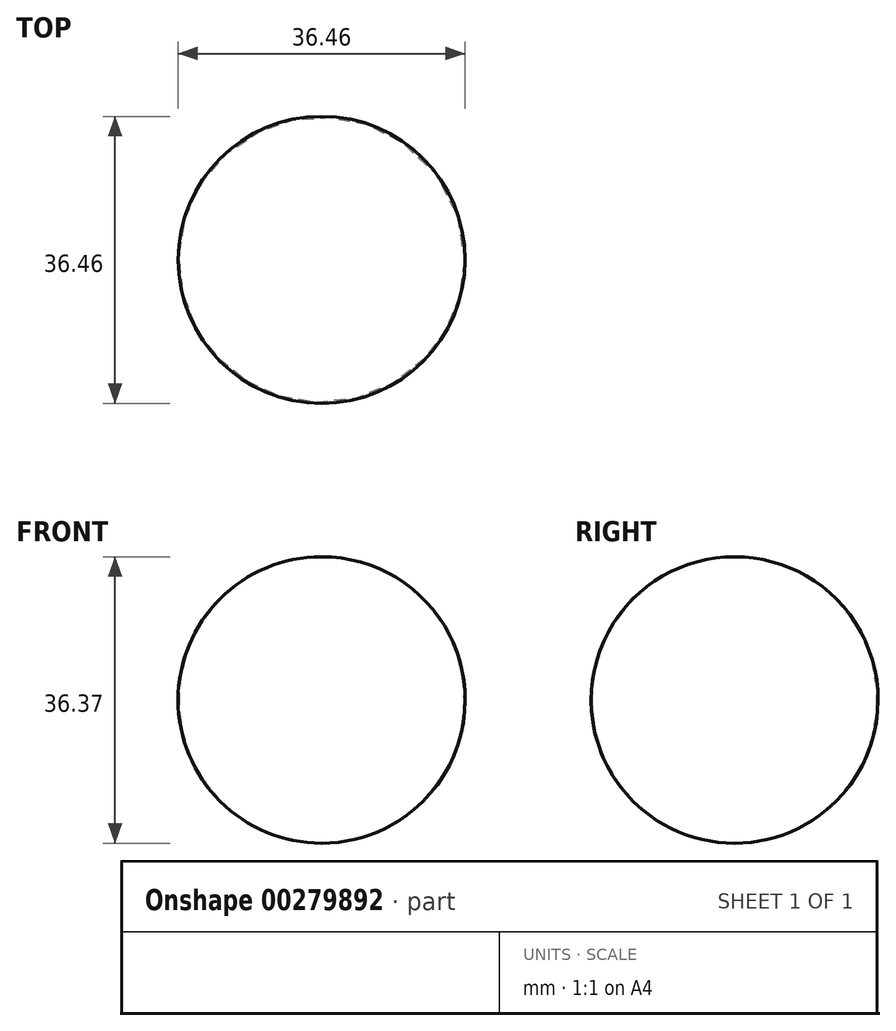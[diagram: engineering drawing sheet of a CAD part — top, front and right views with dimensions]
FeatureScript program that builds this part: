
annotation { "Feature Type Name" : "Feature", "Feature Type Description" : "" }
export const myFeature = defineFeature(function(context is Context, id is Id, definition is map)
    precondition{}
    {
        {
            var Q0;
            Q0=qCreatedBy(makeId("Front.planeOp"),FACE);
            var sketch = newSketch(context, id + "F0", { "sketchPlane" : qUnion([Q0])});
            skLineSegment(sketch, "E0", {"start": v(0, 0) * mm, "end": v(0, 36.37) * mm});
            skArc(sketch, "E1", {"start": v(0, 0) * mm, "mid": v(18.23, 18.19) * mm, "end": v(0, 36.37) * mm});
            skSolve(sketch);
        }
        {
            var Q0;
            Q0 = qSketchRegion(id + "F0", true);
            var Q1;
            Q1=sQuery(id+"F0.wireOp",EDGE,"E0");
            revolve(context, id + "F1", {"entities" : qUnion([Q0]), "axis" : qUnion([Q1]), "revolveType" : RevolveType.FULL});
        }
    });
